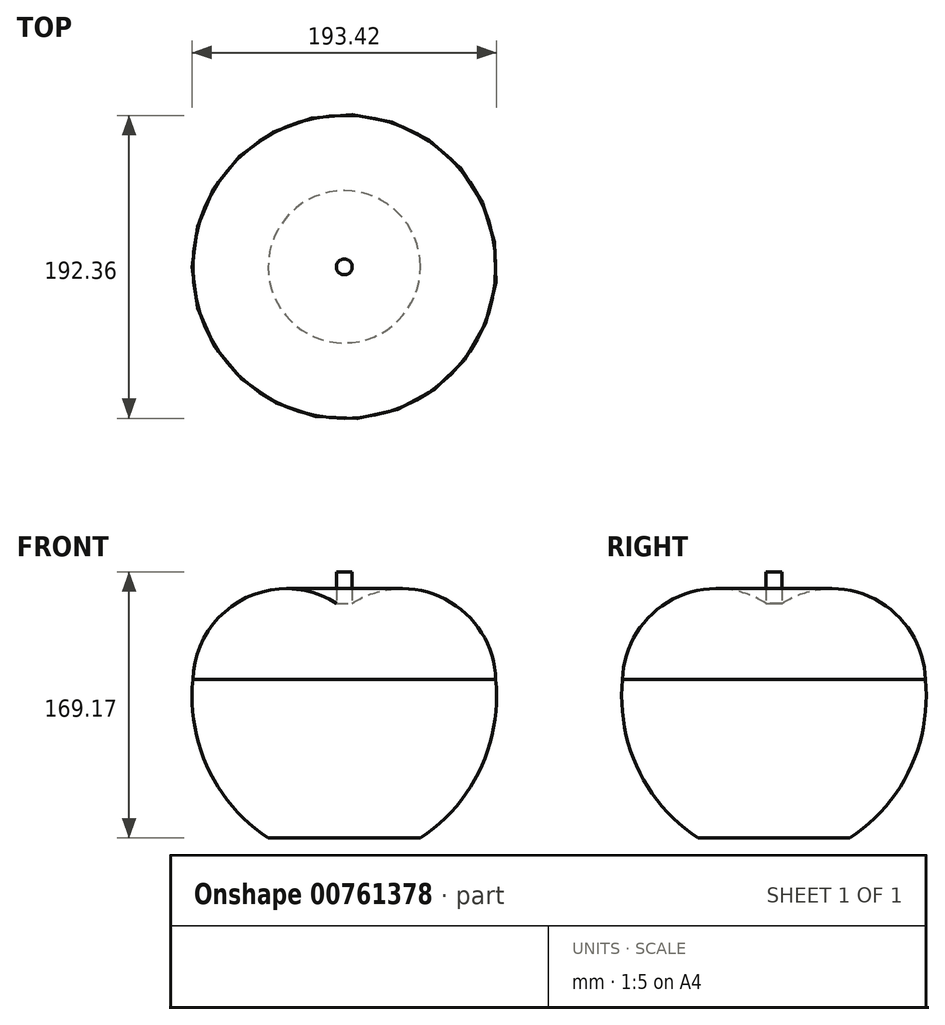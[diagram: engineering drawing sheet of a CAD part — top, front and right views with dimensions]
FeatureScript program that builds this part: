
annotation { "Feature Type Name" : "Feature", "Feature Type Description" : "" }
export const myFeature = defineFeature(function(context is Context, id is Id, definition is map)
    precondition{}
    {
        {
            var Q0;
            Q0=qCreatedBy(makeId("Front.planeOp"),FACE);
            var sketch = newSketch(context, id + "F0", { "sketchPlane" : qUnion([Q0])});
            skLineSegment(sketch, "E0", {"start": v(0, 0) * mm, "end": v(0, 150) * mm});
            skLineSegment(sketch, "E1", {"start": v(0, 150) * mm, "end": v(5, 150) * mm});
            skLineSegment(sketch, "E2", {"start": v(5, 150) * mm, "end": v(5, 130) * mm});
            skArc(sketch, "E3", {"start": v(96.18, 81.56) * mm, "mid": v(64.68, 132.3) * mm, "end": v(5, 130) * mm});
            skArc(sketch, "E4", {"start": v(48.36, -19.17) * mm, "mid": v(86.29, 24.54) * mm, "end": v(96.18, 81.56) * mm});
            skArc(sketch, "E5", {"start": v(0, 0) * mm, "mid": v(17.67, -26) * mm, "end": v(48.36, -19.17) * mm});
            skSolve(sketch);
        }
        {
            var Q0;
            Q0=makeQuery(id+"F0.imprint","IMPRINT",FACE,{"disambiguationData":[TD([[makeQuery(id+"F0.imprint","IMPRINT",EDGE,{"derivedFrom":sQuery(id+"F0.wireOp",EDGE,"E0")}),-1.0]])]});
            var Q1;
            Q1=sQuery(id+"F0.wireOp",EDGE,"E0");
            revolve(context, id + "F1", {"surfaceOperationType" : NewSurfaceOperationType.NEW, "entities" : qUnion([Q0]), "axis" : qUnion([Q1]), "revolveType" : RevolveType.FULL});
        }
    });
